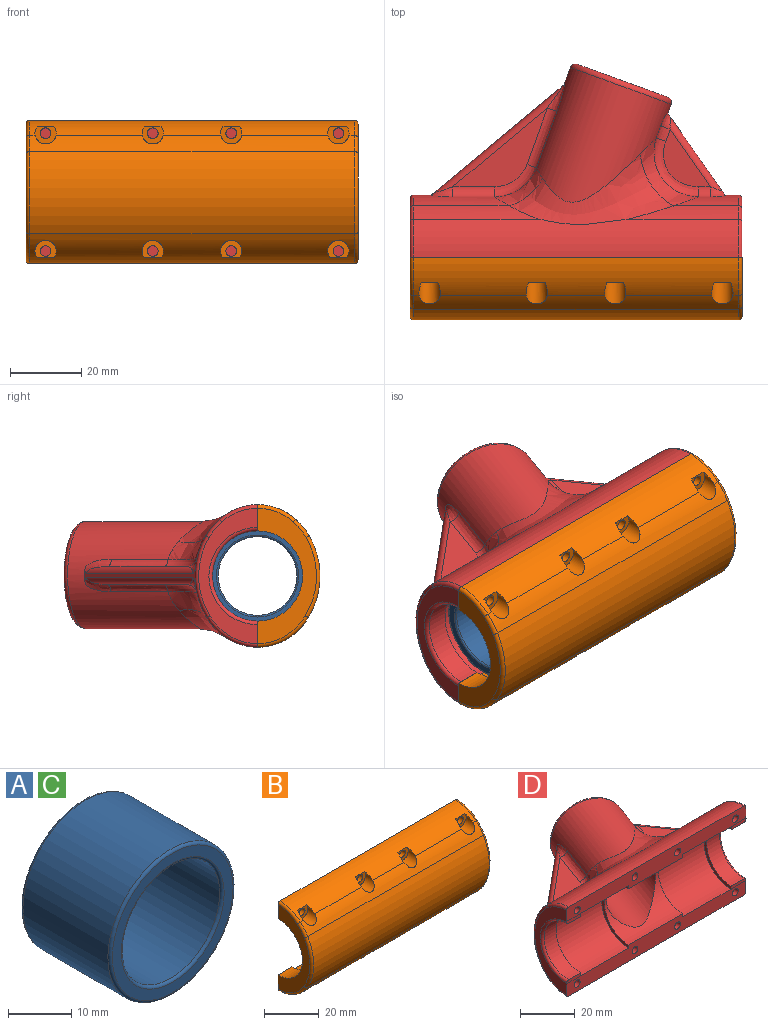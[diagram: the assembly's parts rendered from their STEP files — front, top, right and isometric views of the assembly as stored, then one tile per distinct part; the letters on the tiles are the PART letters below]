
ASSEMBLY  parts=4 mates=3
PART A: 8 faces, bbox 30.3x20x30.3 mm
  f0: cylinder r=11mm len=22mm, axis (0,1,0), area 1313.2mm2, adj f4,f6
  f1: cylinder r=14mm len=28mm, axis (0,1,0), area 1671.3mm2, adj f5,f7
  f2: plane 27x27mm, normal (0,-1,0), area 157.1mm2, adj f6,f7
  f3: plane 27x27mm, normal (0,1,0), area 157.1mm2, adj f4,f5
  f4: torus R=11.5mm, axis (0,-1,0), area 55.2mm2, adj f0,f3
  f5: torus R=13.5mm, axis (0,-1,0), area 68.2mm2, adj f1,f3
  f6: torus R=11.5mm, axis (0,-1,0), area 55.2mm2, adj f0,f2
  f7: torus R=13.5mm, axis (0,-1,0), area 68.2mm2, adj f1,f2
PART B: 50 faces, bbox 93x19.4x42.7 mm
  f0: cylinder r=17.85mm len=91mm, axis (-1,0,0), area 483.8mm2, adj f1,f3,f33,f35,f37,f39,f42,f46
  f1: cylinder r=16.12mm len=91mm, axis (-1,0,0), area 963.4mm2, adj f0,f7,f33,f34,f35,f36,f37,f38
  f2: plane 28x14mm, normal (-1,0,0), area 57.5mm2, adj f5,f7,f12,f13
  f3: cylinder r=22.4mm len=91mm, axis (-1,0,0), area 2194.5mm2, adj f0,f4,f43,f47
  f4: cylinder r=16.74mm len=91mm, axis (-1,0,0), area 1408.2mm2, adj f3,f5,f25,f26,f27,f28,f29,f30
  f5: plane 93.01x7.38mm, normal (0,1,0), area 588.2mm2, adj f2,f4,f6,f8,f9,f10,f11,f12
  f6: cylinder r=14mm len=28mm, axis (-1,0,0), area 1099.6mm2, adj f5,f7,f8,f11
  f7: plane 93x7.38mm, normal (0,1,0), area 588.2mm2, adj f1,f2,f6,f8,f9,f10,f11,f12
  f8: plane 28x14mm, normal (-1,0,0), area 57.5mm2, adj f5,f6,f7,f10
  f9: plane 38x16.5mm, normal (1,0,0), area 201.2mm2, adj f5,f7,f45,f46,f47,f48,f49
  f10: cylinder r=12.63mm len=25.25mm, axis (-1,0,0), area 267.7mm2, adj f5,f7,f8,f49
  f11: plane 28x14mm, normal (1,0,0), area 57.5mm2, adj f5,f6,f7,f12
  f12: cylinder r=12.63mm len=28mm, axis (1,0,0), area 1110.6mm2, adj f2,f5,f7,f11
  f13: cylinder r=14mm len=28mm, axis (1,0,0), area 1099.6mm2, adj f2,f5,f7,f14
  f14: plane 28x14mm, normal (1,0,0), area 57.5mm2, adj f5,f7,f13,f16
  f15: plane 38x16.5mm, normal (-1,0,0), area 242.4mm2, adj f5,f7,f16,f41,f42,f43,f44
  f16: cylinder r=12.63mm len=25.25mm, axis (1,0,0), area 287.6mm2, adj f5,f7,f14,f15
  f17: cylinder r=1.5mm len=7mm, axis (0,1,0), area 66mm2, adj f7,f40
  f18: cylinder r=1.5mm len=7mm, axis (0,1,0), area 66mm2, adj f7,f38
  f19: cylinder r=1.5mm len=7mm, axis (0,1,0), area 66mm2, adj f7,f36
  f20: cylinder r=1.5mm len=7mm, axis (0,1,0), area 66mm2, adj f7,f34
  f21: cylinder r=1.5mm len=7mm, axis (0,1,0), area 66mm2, adj f5,f32
  f22: cylinder r=1.5mm len=7mm, axis (0,1,0), area 66mm2, adj f5,f30
  f23: cylinder r=1.5mm len=7mm, axis (0,1,0), area 66mm2, adj f5,f28
  f24: cylinder r=1.5mm len=7mm, axis (0,1,0), area 66mm2, adj f5,f26
  f25: cylinder r=3mm len=6mm, axis (0,-1,0), area 52.5mm2, adj f4,f26
  f26: plane 6x4.8mm, normal (0,-1,0), area 17.2mm2, adj f4,f24,f25
  f27: cylinder r=3mm len=6mm, axis (0,-1,0), area 52.5mm2, adj f4,f28
  f28: plane 6x4.8mm, normal (0,-1,0), area 17.2mm2, adj f4,f23,f27
  f29: cylinder r=3mm len=6mm, axis (0,-1,0), area 52.5mm2, adj f4,f30
  f30: plane 6x4.8mm, normal (0,-1,0), area 17.2mm2, adj f4,f22,f29
  f31: cylinder r=3mm len=6mm, axis (0,-1,0), area 52.5mm2, adj f4,f32
  f32: plane 6x4.8mm, normal (0,-1,0), area 17.2mm2, adj f4,f21,f31
  f33: cylinder r=3mm len=6mm, axis (0,-1,0), area 53.3mm2, adj f0,f1,f34
  f34: plane 6x4.89mm, normal (0,-1,0), area 17.6mm2, adj f1,f20,f33
  f35: cylinder r=3mm len=6mm, axis (0,-1,0), area 53.3mm2, adj f0,f1,f36
  f36: plane 6x4.89mm, normal (0,-1,0), area 17.6mm2, adj f1,f19,f35
  f37: cylinder r=3mm len=6mm, axis (0,-1,0), area 53.3mm2, adj f0,f1,f38
  f38: plane 6x4.89mm, normal (0,-1,0), area 17.6mm2, adj f1,f18,f37
  f39: cylinder r=3mm len=6mm, axis (0,-1,0), area 53.3mm2, adj f0,f1,f40
  f40: plane 6x4.89mm, normal (0,-1,0), area 17.6mm2, adj f1,f17,f39
  f41: torus R=15.12mm, axis (-1,0,0), area 17.9mm2, adj f1,f7,f15,f42
  f42: torus R=16.85mm, axis (-1,0,0), area 9.2mm2, adj f0,f15,f41,f43
  f43: torus R=21.4mm, axis (-1,0,0), area 37.3mm2, adj f3,f15,f42,f44
  f44: torus R=15.74mm, axis (-1,0,0), area 26.5mm2, adj f4,f5,f15,f43
  f45: torus R=15.12mm, axis (1,0,0), area 17.9mm2, adj f1,f7,f9,f46
  f46: torus R=16.85mm, axis (1,0,0), area 9.2mm2, adj f0,f9,f45,f47
  f47: torus R=21.4mm, axis (1,0,0), area 37.3mm2, adj f3,f9,f46,f48
  f48: torus R=15.74mm, axis (1,0,0), area 26.5mm2, adj f4,f5,f9,f47
  f49: torus R=13.63mm, axis (1,0,0), area 64.1mm2, adj f5,f7,f9,f10
PART C: same geometry as A
PART D: 98 faces, bbox 93.3x64.9x43 mm
  f0: bspline ~20.96x19.7mm, area 174.8mm2, adj f6,f41,f45,f90
  f1: bspline ~14.91x12.17mm, area 99.2mm2, adj f10,f41,f45,f80
  f2: cylinder r=17.85mm len=31.24mm, axis (1,0,0), area 147.3mm2, adj f6,f9,f46,f65
  f3: cylinder r=12.62mm len=28mm, axis (-1,0,0), area 531.3mm2, adj f8,f12,f13,f14,f43
  f4: cylinder r=14mm len=28mm, axis (1,0,0), area 1099.6mm2, adj f8,f12,f13,f20
  f5: cylinder r=17.85mm len=35.19mm, axis (1,0,0), area 185.1mm2, adj f9,f10,f46,f69
  f6: cylinder r=22.4mm len=22.97mm, axis (1,0,0), area 247.3mm2, adj f0,f2,f7,f44,f45,f46,f57,f60
  f7: cylinder r=16.74mm len=91mm, axis (1,0,0), area 1349mm2, adj f6,f10,f12,f45,f63,f71
  f8: plane 93x7.38mm, normal (0,-1,0), area 567.8mm2, adj f3,f4,f9,f11,f13,f14,f15,f18
  f9: cylinder r=16.12mm len=91mm, axis (1,0,0), area 1035.7mm2, adj f2,f5,f8,f46,f66,f68
  f10: cylinder r=22.4mm len=27.62mm, axis (1,0,0), area 409.6mm2, adj f1,f5,f7,f45,f46,f47,f49,f52
  f11: cylinder r=14mm len=28mm, axis (1,0,0), area 1099.6mm2, adj f8,f12,f14,f19
  f12: plane 93.01x7.38mm, normal (0,-1,0), area 567.8mm2, adj f3,f4,f7,f11,f13,f14,f15,f16
  f13: plane 28x14mm, normal (1,0,0), area 57.5mm2, adj f3,f4,f8,f12
  f14: plane 28x14mm, normal (-1,0,0), area 57.5mm2, adj f3,f8,f11,f12
  f15: plane 38x16.5mm, normal (-1,0,0), area 201.2mm2, adj f8,f12,f16,f18,f68,f69,f70,f71
  f16: plane 7.25x1.38mm, normal (0,-1,0), area 9.8mm2, adj f12,f15,f17,f19,f72
  f17: cylinder r=12.62mm len=25.25mm, axis (1,0,0), area 247.9mm2, adj f16,f18,f19,f72
  f18: plane 7.25x1.38mm, normal (0,-1,0), area 9.8mm2, adj f8,f15,f17,f19,f72
  f19: plane 28x14mm, normal (1,0,0), area 57.5mm2, adj f11,f16,f17,f18
  f20: plane 28x14mm, normal (-1,0,0), area 57.5mm2, adj f4,f22,f23,f24
  f21: plane 38x16.5mm, normal (1,0,0), area 201.2mm2, adj f8,f12,f22,f24,f63,f64,f65,f66
  f22: plane 7.75x1.38mm, normal (0,-1,0), area 10.4mm2, adj f8,f20,f21,f23,f67
  f23: cylinder r=12.62mm len=25.25mm, axis (-1,0,0), area 267.7mm2, adj f20,f22,f24,f67
  f24: plane 7.75x1.38mm, normal (0,-1,0), area 10.4mm2, adj f12,f20,f21,f23,f67
  f25: cylinder r=1.5mm len=6.15mm, axis (0,-1,0), area 57.9mm2, adj f12,f26
  f26: plane 3x3mm, normal (0,-1,0), area 7.1mm2, adj f25
  f27: cylinder r=1.5mm len=6.15mm, axis (0,-1,0), area 57.9mm2, adj f12,f28
  f28: plane 3x3mm, normal (0,-1,0), area 7.1mm2, adj f27
  f29: cylinder r=1.5mm len=6.15mm, axis (0,-1,0), area 57.9mm2, adj f12,f30
  f30: plane 3x3mm, normal (0,-1,0), area 7.1mm2, adj f29
  f31: cylinder r=1.5mm len=6.15mm, axis (0,-1,0), area 57.9mm2, adj f12,f32
  f32: plane 3x3mm, normal (0,-1,0), area 7.1mm2, adj f31
  f33: cylinder r=1.5mm len=6.15mm, axis (0,-1,0), area 57.9mm2, adj f8,f34
  f34: plane 3x3mm, normal (0,-1,0), area 7.1mm2, adj f33
  f35: cylinder r=1.5mm len=6.15mm, axis (0,-1,0), area 57.9mm2, adj f8,f36
  f36: plane 3x3mm, normal (0,-1,0), area 7.1mm2, adj f35
  f37: cylinder r=1.5mm len=6.15mm, axis (0,-1,0), area 57.9mm2, adj f8,f38
  f38: plane 3x3mm, normal (0,-1,0), area 7.1mm2, adj f37
  f39: cylinder r=1.5mm len=6.15mm, axis (0,-1,0), area 57.9mm2, adj f8,f40
  f40: plane 3x3mm, normal (0,-1,0), area 7.1mm2, adj f39
  f41: cylinder r=15mm len=43.71mm, axis (0.34,0.94,0), area 2161.6mm2, adj f0,f1,f44,f45,f46,f47,f50,f53
  f42: plane 27x25.37mm, normal (0.34,0.94,0), area 41.6mm2, adj f62,f73
  f43: cylinder r=12mm len=48.24mm, axis (0.34,0.94,0), area 3212.2mm2, adj f3,f73
  f44: bspline ~20.38x18.37mm, area 157.4mm2, adj f6,f41,f46,f95
  f45: bspline ~47.26x20.35mm, area 435.5mm2, adj f0,f1,f6,f7,f10,f41
  f46: bspline ~49.36x21.78mm, area 448.7mm2, adj f2,f5,f6,f9,f10,f41,f44,f47
  f47: bspline ~14.38x11.8mm, area 90.1mm2, adj f10,f41,f46,f85
  f48: plane 26.51x22.06mm, normal (0,0,1), area 195.8mm2, adj f76,f84,f85,f86
  f49: plane 3.2x0.36mm, normal (-0.77,-0.64,0), area 0.1mm2, adj f10,f54,f87
  f50: plane 2.41x0.28mm, normal (0.77,0.64,0), area 0.1mm2, adj f41,f54,f83
  f51: plane 26.55x22.09mm, normal (0,0,-1), area 196.4mm2, adj f77,f79,f80,f81
  f52: plane 2.87x0.29mm, normal (-0.77,-0.64,0), area 0.1mm2, adj f10,f54,f82
  f53: plane 2.72x0.36mm, normal (0.77,0.64,0), area 0.1mm2, adj f41,f54,f78
  f54: plane 37.35x31.11mm, normal (-0.64,0.77,0), area 50.2mm2, adj f10,f41,f49,f50,f52,f53,f76,f77
  f55: plane 16.08x13.18mm, normal (0,0,-1), area 97.7mm2, adj f75,f89,f90,f91
  f56: plane 4.23x1.09mm, normal (-0.57,0.82,0), area 0.4mm2, adj f41,f61,f88
  f57: plane 3.78x0.64mm, normal (0.57,-0.82,0), area 0.3mm2, adj f6,f61,f92
  f58: plane 16.07x13.15mm, normal (0,0,1), area 97.5mm2, adj f74,f94,f95,f96
  f59: plane 3.92x0.94mm, normal (-0.57,0.82,0), area 0.4mm2, adj f41,f61,f93
  f60: plane 4.12x0.75mm, normal (0.57,-0.82,0), area 0.3mm2, adj f6,f61,f97
  f61: plane 23.18x16.31mm, normal (0.82,0.57,0), area 32.7mm2, adj f6,f41,f56,f57,f59,f60,f74,f75
  f62: torus R=13.5mm, axis (-0.34,-0.94,0), area 214mm2, adj f41,f42
  f63: torus R=15.74mm, axis (1,0,0), area 26.5mm2, adj f7,f12,f21,f64
  f64: torus R=21.4mm, axis (1,0,0), area 37.3mm2, adj f6,f21,f63,f65
  f65: torus R=16.85mm, axis (1,0,0), area 9.2mm2, adj f2,f21,f64,f66
  f66: torus R=15.12mm, axis (1,0,0), area 17.9mm2, adj f8,f9,f21,f65
  f67: torus R=13.62mm, axis (1,0,0), area 64.1mm2, adj f21,f22,f23,f24
  f68: torus R=15.12mm, axis (-1,0,0), area 17.9mm2, adj f8,f9,f15,f69
  f69: torus R=16.85mm, axis (-1,0,0), area 9.2mm2, adj f5,f15,f68,f70
  f70: torus R=21.4mm, axis (-1,0,0), area 37.3mm2, adj f10,f15,f69,f71
  f71: torus R=15.74mm, axis (-1,0,0), area 26.5mm2, adj f7,f12,f15,f70
  f72: torus R=13.62mm, axis (-1,0,0), area 64.1mm2, adj f15,f16,f17,f18
  f73: cone r=13mm half-angle=45deg, axis (0.34,0.94,0), area 111.1mm2, adj f42,f43
  f74: cylinder r=2mm len=21.5mm, axis (-0.57,0.82,0), area 69.8mm2, adj f58,f61,f93,f97
  f75: cylinder r=2mm len=21.5mm, axis (0.57,-0.82,0), area 69.9mm2, adj f55,f61,f88,f92
  f76: cylinder r=2mm len=37mm, axis (-0.77,-0.64,0), area 127.2mm2, adj f48,f54,f83,f87
  f77: cylinder r=2mm len=37mm, axis (0.77,0.64,0), area 127.3mm2, adj f51,f54,f78,f82
  f78: bspline ~9.56x5.69mm, area 20.8mm2, adj f41,f53,f54,f77,f79
  f79: bspline ~61.96x24.87mm, area 63.5mm2, adj f41,f51,f78,f80
  f80: bspline ~13.7x10.24mm, area 51.5mm2, adj f1,f51,f79,f81
  f81: cylinder r=3mm len=11.71mm, axis (1,0,0), area 47.7mm2, adj f10,f51,f80,f82
  f82: bspline ~8.72x4.88mm, area 19.1mm2, adj f10,f52,f54,f77,f81
  f83: bspline ~9.65x5.78mm, area 21.3mm2, adj f41,f50,f54,f76,f84
  f84: bspline ~61.92x24.87mm, area 64mm2, adj f41,f48,f83,f85
  f85: bspline ~13.68x10.25mm, area 51.5mm2, adj f47,f48,f84,f86
  f86: cylinder r=3mm len=11.71mm, axis (1,0,0), area 47.3mm2, adj f10,f48,f85,f87
  f87: bspline ~8.68x4.83mm, area 18.8mm2, adj f10,f49,f54,f76,f86
  f88: bspline ~6.34x4.78mm, area 12.9mm2, adj f41,f56,f61,f75,f89
  f89: bspline ~18.2x8.95mm, area 13.8mm2, adj f41,f55,f88,f90
  f90: bspline ~18.06x14.16mm, area 71.8mm2, adj f0,f55,f89,f91
  f91: cylinder r=3mm len=3.29mm, axis (1,0,0), area 13.4mm2, adj f6,f55,f90,f92
  f92: bspline ~6.07x4.78mm, area 14.7mm2, adj f6,f57,f61,f75,f91
  f93: bspline ~6.4x4.83mm, area 13.2mm2, adj f41,f59,f61,f74,f94
  f94: bspline ~17.95x8.87mm, area 13.7mm2, adj f41,f58,f93,f95
  f95: bspline ~18.09x14.11mm, area 71.9mm2, adj f44,f58,f94,f96
  f96: cylinder r=3mm len=3.32mm, axis (1,0,0), area 13.4mm2, adj f6,f58,f95,f97
  f97: bspline ~6.04x4.75mm, area 14.4mm2, adj f6,f60,f61,f74,f96
PLACE A rot(axis=(0,0,-1),90deg) t=(-17.86,-6.77,31.41)mm
PLACE B t=(-1.11,-6.77,11.41)mm
PLACE C rot(axis=(0,0,1),90deg) t=(15.14,-6.77,31.41)mm
PLACE D t=(-1.11,-6.77,11.41)mm fixed
MATE revolute A.f1 <-> D.f4  axis (1,0,0) through (-27.86,-6.77,31.41)mm
MATE revolute C.f1 <-> D.f4  axis (-1,0,0) through (25.14,-6.77,31.41)mm
MATE fastened B.f22 <-> D.f31  axis (0,1,0) through (39.89,-6.77,14.86)mm
